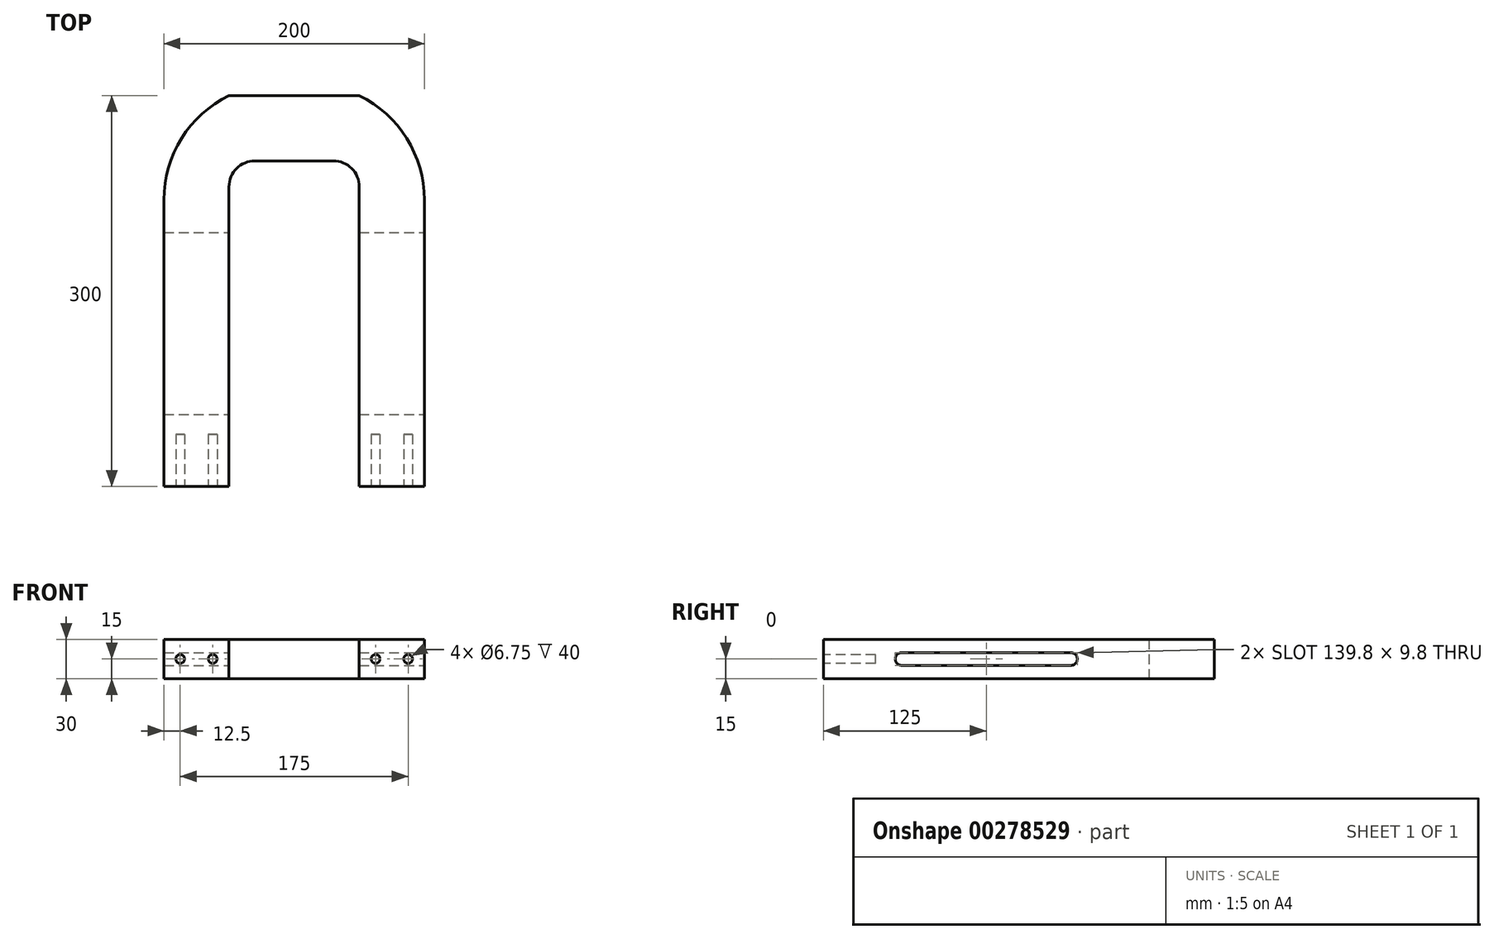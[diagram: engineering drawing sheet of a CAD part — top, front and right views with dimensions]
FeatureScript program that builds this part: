
annotation { "Feature Type Name" : "Feature", "Feature Type Description" : "" }
export const myFeature = defineFeature(function(context is Context, id is Id, definition is map)
    precondition{}
    {
        {
            var Q0;
            Q0=qCreatedBy(makeId("Top.planeOp"),FACE);
            var sketch = newSketch(context, id + "F0", { "sketchPlane" : qUnion([Q0])});
            skLineSegment(sketch, "E0.bottom", {"start": v(50, -150) * mm, "end": v(-50, -150) * mm, "construction": true});
            skLineSegment(sketch, "E0.top", {"start": v(50, 150) * mm, "end": v(-50, 150) * mm});
            skLineSegment(sketch, "E0.left", {"start": v(50, -150) * mm, "end": v(50, 150) * mm});
            skLineSegment(sketch, "E0.right", {"start": v(-50, -150) * mm, "end": v(-50, 100) * mm});
            skPoint(sketch, "E0.middle", {"position": v(0, 0) * mm});
            skLineSegment(sketch, "E1", {"start": v(-100, -150) * mm, "end": v(-100, 70) * mm});
            skLineSegment(sketch, "E2", {"start": v(-100, -150) * mm, "end": v(-50, -150) * mm});
            skLineSegment(sketch, "E3", {"start": v(50, -150) * mm, "end": v(100, -150) * mm});
            skLineSegment(sketch, "E4", {"start": v(100, -150) * mm, "end": v(100, 70) * mm});
            skLineSegment(sketch, "E5", {"start": v(-50, 100) * mm, "end": v(50, 100) * mm});
            skLineSegment(sketch, "E6", {"start": v(-50, 100) * mm, "end": v(-50, 150) * mm});
            skArc(sketch, "E7", {"start": v(-50, 150) * mm, "mid": v(-86.47, 117.17) * mm, "end": v(-100, 70) * mm});
            skArc(sketch, "E8", {"start": v(100, 70) * mm, "mid": v(86.47, 117.17) * mm, "end": v(50, 150) * mm});
            skSolve(sketch);
        }
        {
            var Q0;
            Q0=makeQuery(id+"F0.imprint","IMPRINT",FACE,{"disambiguationData":[TD([[makeQuery(id+"F0.imprint","IMPRINT",EDGE,{"derivedFrom":sQuery(id+"F0.wireOp",EDGE,"E0.right")}),1.0]])]});
            var Q1;
            {var subQ0=sQuery(id+"F0.wireOp",EDGE,"E0.top");Q1=makeQuery(id+"F0.imprint","IMPRINT",FACE,{"disambiguationData":[TD([[makeQuery(id+"F0.imprint","IMPRINT",EDGE,{"derivedFrom":subQ0}),1.0]])]});}
            var Q2;
            {var subQ3=sQuery(id+"F0.wireOp",EDGE,"E3");Q2=makeQuery(id+"F0.imprint","IMPRINT",FACE,{"disambiguationData":[TD([[makeQuery(id+"F0.imprint","IMPRINT",EDGE,{"derivedFrom":subQ3}),1.0]])]});}
            extrude(context, id + "F1", {"entities" : qUnion([Q0, Q1, Q2]), "depth" : 30 * mm});
        }
        {
            var Q0;
            Q0=makeQuery(id+"F1.opExtrude","SWEPT_EDGE",EDGE,{"disambiguationData":[OSD([sQuery(id+"F0.wireOp",EDGE,"E0.right"),sQuery(id+"F0.wireOp",EDGE,"E5"),sQuery(id+"F0.wireOp",EDGE,"E6")])]});
            var Q1;
            Q1=makeQuery(id+"F1.opExtrude","SWEPT_EDGE",EDGE,{"disambiguationData":[OSD([sQuery(id+"F0.wireOp",EDGE,"E0.left"),sQuery(id+"F0.wireOp",EDGE,"E5")])]});
            fillet(context, id + "F2", {"entities" : qUnion([Q0, Q1]), "radius" : 20 * mm, "tangentPropagation" : true, "allowEdgeOverflow" : false});
        }
        {
            var Q0;
            Q0=makeQuery(id+"F1.opExtrude","SWEPT_FACE",FACE,{"disambiguationData":[OSD([sQuery(id+"F0.wireOp",EDGE,"E2")])]});
            var sketch = newSketch(context, id + "F3", { "sketchPlane" : qUnion([Q0])});
            skLineSegment(sketch, "E9", {"start": v(-100, 15) * mm, "end": v(204.6, 15) * mm, "construction": true});
            skPoint(sketch, "E9.endSnap0", {"position": v(-50, 15) * mm});
            skCircle(sketch, "E10", {"center": v(-87.5, 15) * mm, "radius": 3.37 * mm});
            skCircle(sketch, "E11", {"center": v(-62.5, 15) * mm, "radius": 3.37 * mm});
            skCircle(sketch, "E12", {"center": v(62.5, 15) * mm, "radius": 3.37 * mm});
            skCircle(sketch, "E13", {"center": v(87.5, 15) * mm, "radius": 3.37 * mm});
            skSolve(sketch);
        }
        {
            var Q0;
            Q0 = qSketchRegion(id + "F3", true);
            extrude(context, id + "F4", {"entities" : qUnion([Q0]), "operationType" : NewBodyOperationType.REMOVE, "oppositeDirection" : true, "depth" : 40 * mm});
        }
        {
            var Q0;
            Q0=makeQuery(id+"F1.opExtrude","SWEPT_FACE",FACE,{"disambiguationData":[OSD([sQuery(id+"F0.wireOp",EDGE,"E4")])]});
            var sketch = newSketch(context, id + "F5", { "sketchPlane" : qUnion([Q0])});
            skLineSegment(sketch, "E14.bottom", {"start": v(40, 10.1) * mm, "end": v(-90, 10.1) * mm});
            skLineSegment(sketch, "E14.top", {"start": v(40, 19.9) * mm, "end": v(-90, 19.9) * mm});
            skLineSegment(sketch, "E14.left", {"start": v(40, 10.1) * mm, "end": v(40, 19.9) * mm, "construction": true});
            skLineSegment(sketch, "E14.right", {"start": v(-90, 10.1) * mm, "end": v(-90, 19.9) * mm, "construction": true});
            skPoint(sketch, "E14.middle", {"position": v(-25, 15) * mm});
            skLineSegment(sketch, "E15", {"start": v(-150, 15) * mm, "end": v(70, 15) * mm, "construction": true});
            skArc(sketch, "E16", {"start": v(40, 10.1) * mm, "mid": v(44.9, 15) * mm, "end": v(40, 19.9) * mm});
            skArc(sketch, "E17", {"start": v(-90, 19.9) * mm, "mid": v(-94.9, 15) * mm, "end": v(-90, 10.1) * mm});
            skSolve(sketch);
        }
        {
            var Q0;
            Q0=makeQuery(id+"F5.imprint","IMPRINT",FACE,{"disambiguationData":[TD([[makeQuery(id+"F5.imprint","IMPRINT",EDGE,{"derivedFrom":sQuery(id+"F5.wireOp",EDGE,"E14.bottom")}),-1.0]])]});
            var Q1;
            Q1=sQuery(id+"F5.wireOp",EDGE,"E14.left");
            var Q2;
            Q2=sQuery(id+"F5.wireOp",EDGE,"E14.right");
            extrude(context, id + "F6", {"entities" : qUnion([Q0]), "operationType" : NewBodyOperationType.REMOVE, "surfaceEntities" : qUnion([Q1, Q2]), "endBound" : BoundingType.THROUGH_ALL, "oppositeDirection" : true, "depth" : 25 * mm});
        }
    });
